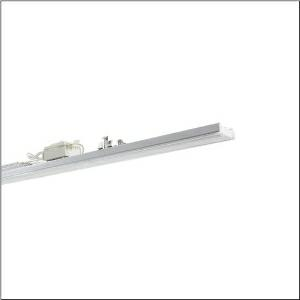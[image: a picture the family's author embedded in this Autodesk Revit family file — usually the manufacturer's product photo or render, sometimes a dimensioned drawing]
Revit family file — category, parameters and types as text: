
# Revit family: licross_21_recessed_mo_52tl14dv4exg
name_source: partatom
category: Lighting Fixtures
units: mm (PartAtom-declared; Revit-internal decimal feet)

## family parameters
Cut with Voids When Loaded = No
Host = Face
Light Source = No
Part Type = Normal
Room Calculation Point = No
Round Connector Dimension = Use Diameter
Shared = No

## types (1)
- --- (1 x LED, 14200 lm, 85.3 W, 4000K)
    Apparent Load = 85 VA
    CIE Flux Codes = 56 84 97 100 100
    Color Rendering = 80
    Color Temperature = 4000K
    Default Elevation = 1800 mm
    Description = Licross 21 Recessed MO, luminaire insert, of sheet steel, galvanised, coil coated, white, length: 2.250mm, width: 66mm, height: 67mm, LED rated luminous flux: 14.200lm, light colour: 840, SDCM (Standard Deviation of Colour Matching)MacAdam ≤ 3 SDCM (initial), control gear: DALI 2, with plug, 5-pole, with phase selection, mains connection: 220..240V, AC, 50/60Hz, rated input power: 85W, internal wiring halogen-free, primary light control with lens, of plastic, primary optical cover: cover, of PMMA, light emission: direct distribution, primary light characteristic: asymmetric, protection rating (complete): IP40, insulation class (complete): insulation class I (protective earthing), certification: CE, ENEC, VDE, UKCA, protection symbol: D if used in an environment without relevant dust loads with corresponding accessories, impact resistance: IK06, permissible ambient temperature for indoor applications: -25..+35°C, corresponds to IFS (International Featured Standards) requirements for safety and quality in the food industry, reducing of maximum allowable ambient temperature of 5°C with ceiling mounting, LABS conformity tested according to VDMA 24364:2018-05, The light source and the operating device comply with the requirements of the Ecodesign Regulation (EU) 2019/2020 and are replaceable in accordance with this regulation, packaging unit: 1 piece
    Height = 58 mm
    Lamp = 1 x LED
    Lamp Light Flux = 14200 lm
    Lamp Power = 85.3 W
    Lamp count = 1
    Length = 2250 mm
    Luminous efficacy = 166 lm/W
    Manufacturer = Siteco
    ModVariant = No
    Model = 52TL14DV4EXG
    Mounting Place = Ceiling
    Mounting Type = Pendant
    Number of Poles = 1
    OnlyDefault = Yes
    Power Factor = 1
    Product Name = Licross 21 Recessed MO
    Product group = luminaire insert | ceiling pendant
    ProductGroupID = 901
    Protection Class = Protection class I
    Protection Degree = IP 40
    RLX_Detail_Level = 1
    RLX_Emergency_Light_Flux = 0 lm
    RLX_Emergency_Type = 0
    RLX_Emergency_Type_DB = No
    RlxData = <blob elided: 30333 chars, md5=07fef784>
    Socket = socket
    Standby Power = 0 W
    System Light Flux = 14200 lm
    System Power = 85 W
    Type Comments = factory setting: luminous flux: 100 % | dim-lin: 254 | 390 mA
    Type Image = l_1296930.jpg
    URL = http://relux.com
    VarID = @adj_128009
    Voltage = 0 V
    Weight = 0.00 kg
    Width = 66 mm

## geometry (parser evidence)
native form markers: Blend x4, Sweep x13
no freeform markers — native parametric forms only
